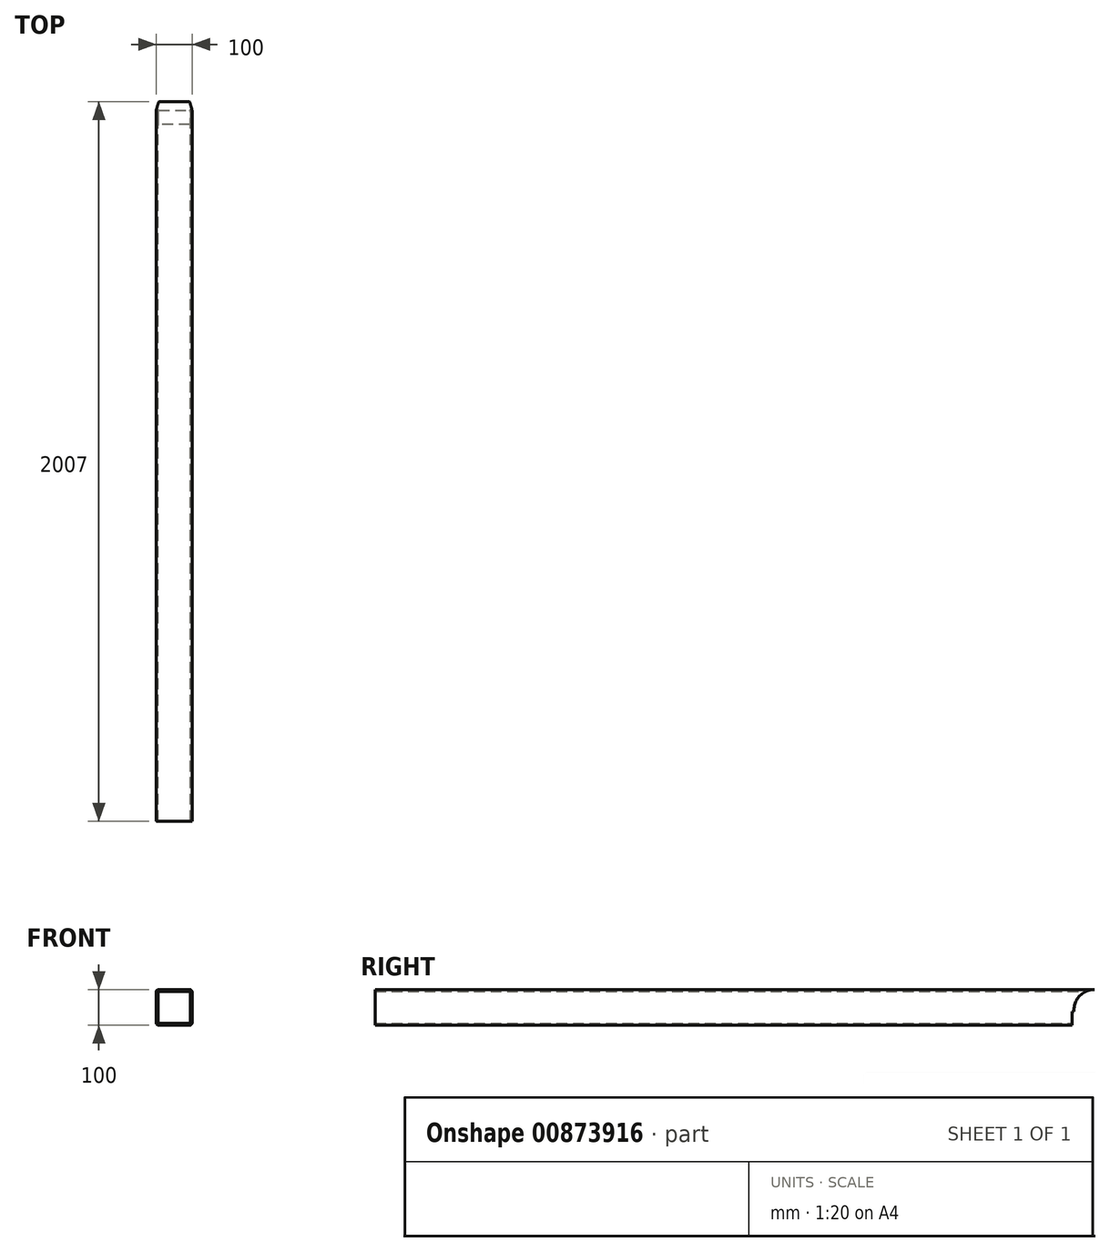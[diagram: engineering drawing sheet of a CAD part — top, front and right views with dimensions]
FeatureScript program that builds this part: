
annotation { "Feature Type Name" : "Feature", "Feature Type Description" : "" }
export const myFeature = defineFeature(function(context is Context, id is Id, definition is map)
    precondition{}
    {
        {
            var Q0;
            Q0=qCreatedBy(makeId("Front.planeOp"),FACE);
            var sketch = newSketch(context, id + "F0", { "sketchPlane" : qUnion([Q0])});
            skLineSegment(sketch, "E0.bottom", {"start": v(43, 50) * mm, "end": v(-43, 50) * mm});
            skLineSegment(sketch, "E0.top", {"start": v(43, -50) * mm, "end": v(-43, -50) * mm});
            skLineSegment(sketch, "E0.left", {"start": v(50, 43) * mm, "end": v(50, -43) * mm});
            skLineSegment(sketch, "E0.right", {"start": v(-50, 43) * mm, "end": v(-50, -43) * mm});
            skPoint(sketch, "E0.middle", {"position": v(0, 0) * mm});
            skPoint(sketch, "E1.visualSharp", {"position": v(-50, 50) * mm});
            skArc(sketch, "E1.filletArc", {"start": v(-43, 50) * mm, "mid": v(-47.95, 47.95) * mm, "end": v(-50, 43) * mm});
            skPoint(sketch, "E2.visualSharp", {"position": v(50, 50) * mm});
            skArc(sketch, "E2.filletArc", {"start": v(50, 43) * mm, "mid": v(47.95, 47.95) * mm, "end": v(43, 50) * mm});
            skPoint(sketch, "E3.visualSharp", {"position": v(-50, -50) * mm});
            skArc(sketch, "E3.filletArc", {"start": v(-50, -43) * mm, "mid": v(-47.95, -47.95) * mm, "end": v(-43, -50) * mm});
            skPoint(sketch, "E4.visualSharp", {"position": v(50, -50) * mm});
            skArc(sketch, "E4.filletArc", {"start": v(43, -50) * mm, "mid": v(47.95, -47.95) * mm, "end": v(50, -43) * mm});
            skLineSegment(sketch, "E5.0", {"start": v(43, -45) * mm, "end": v(-43, -45) * mm});
            skArc(sketch, "E5.1", {"start": v(-45, -43) * mm, "mid": v(-44.41, -44.41) * mm, "end": v(-43, -45) * mm});
            skArc(sketch, "E5.2", {"start": v(43, -45) * mm, "mid": v(44.41, -44.41) * mm, "end": v(45, -43) * mm});
            skLineSegment(sketch, "E5.3", {"start": v(-45, 43) * mm, "end": v(-45, -43) * mm});
            skLineSegment(sketch, "E5.4", {"start": v(45, 43) * mm, "end": v(45, -43) * mm});
            skArc(sketch, "E5.5", {"start": v(45, 43) * mm, "mid": v(44.41, 44.41) * mm, "end": v(43, 45) * mm});
            skLineSegment(sketch, "E5.6", {"start": v(43, 45) * mm, "end": v(-43, 45) * mm});
            skArc(sketch, "E5.7", {"start": v(-43, 45) * mm, "mid": v(-44.41, 44.41) * mm, "end": v(-45, 43) * mm});
            skSolve(sketch);
        }
        {
            var Q0;
            Q0=makeQuery(id+"F0.imprint","IMPRINT",FACE,{"disambiguationData":[TD([[makeQuery(id+"F0.imprint","IMPRINT",EDGE,{"derivedFrom":sQuery(id+"F0.wireOp",EDGE,"E0.bottom")}),1.0]])]});
            extrude(context, id + "F1", {"entities" : qUnion([Q0]), "depth" : 2007 * mm, "offsetDistance" : 25 * mm, "symmetric" : true});
        }
        {
            var Q0;
            Q0=makeQuery(id+"F1.opExtrude","SWEPT_FACE",FACE,{"disambiguationData":[OSD([sQuery(id+"F0.wireOp",EDGE,"E0.left")])]});
            var sketch = newSketch(context, id + "F2", { "sketchPlane" : qUnion([Q0])});
            skArc(sketch, "E6", {"start": v(1003.5, -64.3) * mm, "mid": v(1042.42, 34.7) * mm, "end": v(946.5, -11.3) * mm});
            skLineSegment(sketch, "E7", {"start": v(1003.5, -7.15) * mm, "end": v(1003.5, 50) * mm, "construction": true});
            skLineSegment(sketch, "E8.bottom", {"start": v(946.5, -11.3) * mm, "end": v(940.35, -11.3) * mm});
            skLineSegment(sketch, "E8.right", {"start": v(940.35, -11.3) * mm, "end": v(940.35, -64.3) * mm});
            skLineSegment(sketch, "E9", {"start": v(1003.5, -64.3) * mm, "end": v(940.35, -64.3) * mm});
            skSolve(sketch);
        }
        {
            var Q0;
            Q0 = qSketchRegion(id + "F2", true);
            extrude(context, id + "F3", {"entities" : qUnion([Q0]), "operationType" : NewBodyOperationType.REMOVE, "endBound" : BoundingType.THROUGH_ALL, "oppositeDirection" : true, "depth" : 25 * mm, "offsetDistance" : 25 * mm});
        }
    });
